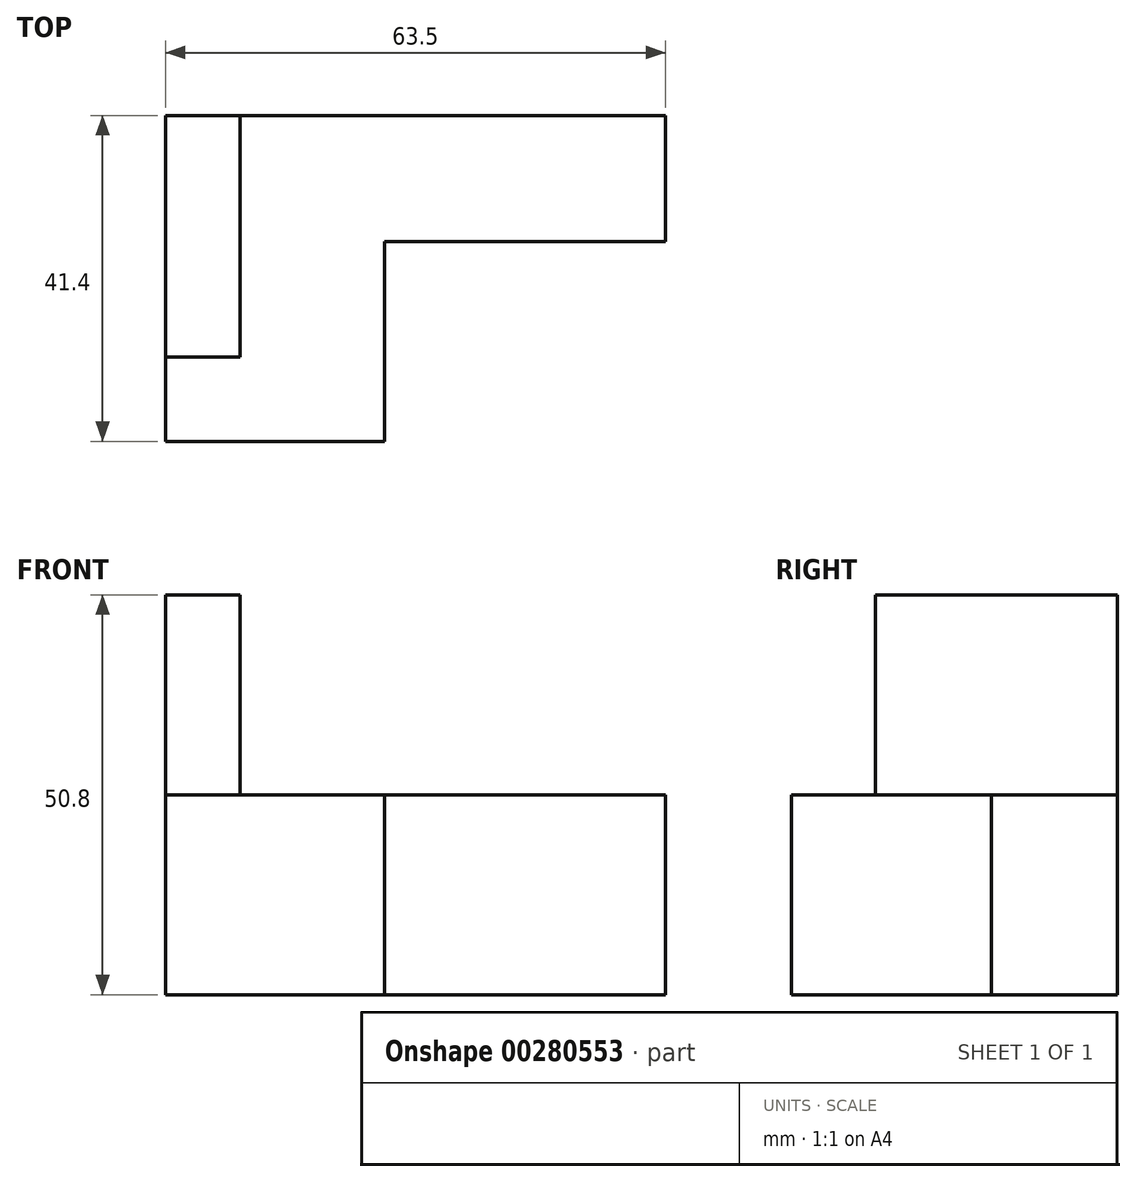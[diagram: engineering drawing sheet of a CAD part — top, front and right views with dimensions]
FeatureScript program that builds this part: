
annotation { "Feature Type Name" : "Feature", "Feature Type Description" : "" }
export const myFeature = defineFeature(function(context is Context, id is Id, definition is map)
    precondition{}
    {
        {
            var Q0;
            Q0=qCreatedBy(makeId("Front.planeOp"),FACE);
            var sketch = newSketch(context, id + "F0", { "sketchPlane" : qUnion([Q0])});
            skLineSegment(sketch, "E0.bottom", {"start": v(-63.5, 25.4) * mm, "end": v(0, 25.4) * mm});
            skLineSegment(sketch, "E0.top", {"start": v(-63.5, 0) * mm, "end": v(0, 0) * mm});
            skLineSegment(sketch, "E0.left", {"start": v(-63.5, 25.4) * mm, "end": v(-63.5, 0) * mm});
            skLineSegment(sketch, "E0.right", {"start": v(0, 25.4) * mm, "end": v(0, 0) * mm});
            skSolve(sketch);
        }
        {
            var Q0;
            Q0=makeQuery(id+"F0.imprint","IMPRINT",FACE,{"disambiguationData":[TD([[makeQuery(id+"F0.imprint","IMPRINT",EDGE,{"derivedFrom":sQuery(id+"F0.wireOp",EDGE,"E0.bottom")}),-1.0]])]});
            extrude(context, id + "F1", {"entities" : qUnion([Q0]), "depth" : 41.4 * mm});
        }
        {
            var Q0;
            Q0=makeQuery(id+"F1.opExtrude","SWEPT_FACE",FACE,{"disambiguationData":[OSD([sQuery(id+"F0.wireOp",EDGE,"E0.bottom")])]});
            var sketch = newSketch(context, id + "F2", { "sketchPlane" : qUnion([Q0])});
            skSolve(sketch);
        }
        {
            var Q0;
            Q0=makeQuery(id+"F1.opExtrude","CAP_FACE",FACE,{"disambiguationData":[OSD([sQuery(id+"F0.wireOp",EDGE,"E0.bottom"),sQuery(id+"F0.wireOp",EDGE,"E0.top"),sQuery(id+"F0.wireOp",EDGE,"E0.left"),sQuery(id+"F0.wireOp",EDGE,"E0.right")])],"isStart":false});
            var sketch = newSketch(context, id + "F3", { "sketchPlane" : qUnion([Q0])});
            skLineSegment(sketch, "E1.bottom", {"start": v(0, 0) * mm, "end": v(-35.66, 0) * mm});
            skLineSegment(sketch, "E1.top", {"start": v(0, 25.4) * mm, "end": v(-35.66, 25.4) * mm});
            skLineSegment(sketch, "E1.left", {"start": v(0, 0) * mm, "end": v(0, 25.4) * mm});
            skLineSegment(sketch, "E1.right", {"start": v(-35.66, 0) * mm, "end": v(-35.66, 25.4) * mm});
            skSolve(sketch);
        }
        {
            var Q0;
            Q0=makeQuery(id+"F3.imprint","IMPRINT",FACE,{"disambiguationData":[TD([[makeQuery(id+"F3.imprint","IMPRINT",EDGE,{"derivedFrom":sQuery(id+"F3.wireOp",EDGE,"E1.bottom")}),1.0]])]});
            extrude(context, id + "F4", {"entities" : qUnion([Q0]), "operationType" : NewBodyOperationType.REMOVE, "oppositeDirection" : true, "depth" : 25.4 * mm});
        }
        {
            var Q0;
            {var subQ0=sQuery(id+"F0.wireOp",EDGE,"E0.bottom");Q0=makeQuery(id+"F2.imprint","IMPRINT",FACE,{"disambiguationData":[TD([[makeQuery(id+"F2.imprint","IMPRINT",EDGE,{"derivedFrom":makeQuery(id+"F1.opExtrude","CAP_EDGE",EDGE,{"disambiguationData":[OSD([subQ0])],"isStart":true})}),-1.0]])]});}
            var sketch = newSketch(context, id + "F5", { "sketchPlane" : qUnion([Q0])});
            skLineSegment(sketch, "E2.bottom", {"start": v(-54.04, 0) * mm, "end": v(-63.52, 0) * mm});
            skLineSegment(sketch, "E2.top", {"start": v(-54.04, -30.71) * mm, "end": v(-63.52, -30.71) * mm});
            skLineSegment(sketch, "E2.left", {"start": v(-54.04, 0) * mm, "end": v(-54.04, -30.71) * mm});
            skLineSegment(sketch, "E2.right", {"start": v(-63.52, 0) * mm, "end": v(-63.52, -30.71) * mm});
            skSolve(sketch);
        }
        {
            var Q0;
            {var subQ4=sQuery(id+"F5.wireOp",EDGE,"E2.left");Q0=makeQuery(id+"F5.imprint","IMPRINT",FACE,{"disambiguationData":[TD([[makeQuery(id+"F5.imprint","IMPRINT",EDGE,{"derivedFrom":subQ4}),-1.0]])]});}
            extrude(context, id + "F6", {"entities" : qUnion([Q0]), "operationType" : NewBodyOperationType.ADD, "depth" : 25.4 * mm});
        }
    });
